# Revit family: Economy_Static_Shelving
name_source: partatom
category: Furniture
revit_build: Autodesk Revit 2016 (Build: 20150714_1515(x64)
units: mm (PartAtom-declared; Revit-internal decimal feet)

## family parameters
Always vertical = Yes
Cut with Voids When Loaded = No
OmniClass Number = 23.40.20.00
OmniClass Title = General Furniture and Specialties
Room Calculation Point = No
Shared = No
Work Plane-Based = No

## types (32) — shared parameters
Manufacturer = BISLEY
Model = Economy Shelving

## per-type parameters (varying)
| type | Depth | Extension | Extension width | Height | Shelving spacing | Width |
| 0818ESSTK30 | 300 mm | No | 800 mm  [stored 2.62467 ft] | 1832 mm  [stored 6.0105 ft] | 333 mm | 832 mm |
| 0818ESSTK30 + 0818ESEXK30 | 300 mm | Yes | 800 mm  [stored 2.62467 ft] | 1832 mm  [stored 6.0105 ft] | 333 mm | 832 mm |
| 0822ESSTK30 | 300 mm | No | 800 mm  [stored 2.62467 ft] | 2192 mm  [stored 7.1916 ft] | 405 mm | 832 mm |
| 0822ESSTK30 + 0822ESEXK30 | 300 mm | Yes | 800 mm  [stored 2.62467 ft] | 2192 mm  [stored 7.1916 ft] | 405 mm | 832 mm |
| 0818ESSTK36 | 360 mm  [stored 1.1811 ft] | No | 800 mm  [stored 2.62467 ft] | 1832 mm  [stored 6.0105 ft] | 333 mm | 832 mm |
| 0818ESSTK36 + 0818ESEXK36 | 360 mm  [stored 1.1811 ft] | Yes | 800 mm  [stored 2.62467 ft] | 1832 mm  [stored 6.0105 ft] | 333 mm | 832 mm |
| 0822ESSTK36 | 360 mm  [stored 1.1811 ft] | No | 800 mm  [stored 2.62467 ft] | 2192 mm  [stored 7.1916 ft] | 405 mm | 832 mm |
| 0822ESSTK36 + 0822ESEXK36 | 360 mm  [stored 1.1811 ft] | Yes | 800 mm  [stored 2.62467 ft] | 2192 mm  [stored 7.1916 ft] | 405 mm | 832 mm |
| 0818ESSTK40 | 400 mm  [stored 1.31234 ft] | No | 800 mm  [stored 2.62467 ft] | 1832 mm  [stored 6.0105 ft] | 333 mm | 832 mm |
| 0818ESSTK40 + 0818ESEXK40 | 400 mm  [stored 1.31234 ft] | Yes | 800 mm  [stored 2.62467 ft] | 1832 mm  [stored 6.0105 ft] | 333 mm | 832 mm |
| 0822ESSTK40 | 400 mm  [stored 1.31234 ft] | No | 800 mm  [stored 2.62467 ft] | 2192 mm  [stored 7.1916 ft] | 405 mm | 832 mm |
| 0822ESSTK40 + 0822ESEXK40 | 400 mm  [stored 1.31234 ft] | Yes | 800 mm  [stored 2.62467 ft] | 2192 mm  [stored 7.1916 ft] | 405 mm | 832 mm |
| 0818ESSTK46 | 460 mm  [stored 1.50919 ft] | No | 800 mm  [stored 2.62467 ft] | 1832 mm  [stored 6.0105 ft] | 333 mm | 832 mm |
| 0818ESSTK46 + 0818ESEXK46 | 460 mm  [stored 1.50919 ft] | Yes | 800 mm  [stored 2.62467 ft] | 1832 mm  [stored 6.0105 ft] | 333 mm | 832 mm |
| 0822ESSTK46 | 460 mm  [stored 1.50919 ft] | No | 800 mm  [stored 2.62467 ft] | 2192 mm  [stored 7.1916 ft] | 405 mm | 832 mm |
| 0822ESSTK46 + 0822ESEXK46 | 460 mm  [stored 1.50919 ft] | Yes | 800 mm  [stored 2.62467 ft] | 2192 mm  [stored 7.1916 ft] | 405 mm | 832 mm |
| 1018ESSTK30 | 300 mm | No | 1000 mm  [stored 3.28084 ft] | 1832 mm  [stored 6.0105 ft] | 333 mm | 1032 mm  [stored 3.38583 ft] |
| 1018ESSTK30 + 1018ESEXK30 | 300 mm | Yes | 1000 mm  [stored 3.28084 ft] | 1832 mm  [stored 6.0105 ft] | 333 mm | 1032 mm  [stored 3.38583 ft] |
| 1022ESSTK30 | 300 mm | No | 1000 mm  [stored 3.28084 ft] | 2192 mm  [stored 7.1916 ft] | 405 mm | 1032 mm  [stored 3.38583 ft] |
| 1022ESSTK30 + 1022ESEXK30 | 300 mm | Yes | 1000 mm  [stored 3.28084 ft] | 2192 mm  [stored 7.1916 ft] | 405 mm | 1032 mm  [stored 3.38583 ft] |
| 1018ESSTK36 | 360 mm  [stored 1.1811 ft] | No | 1000 mm  [stored 3.28084 ft] | 1832 mm  [stored 6.0105 ft] | 333 mm | 1032 mm  [stored 3.38583 ft] |
| 1018ESSTK36 + 1018ESEXK36 | 360 mm  [stored 1.1811 ft] | Yes | 1000 mm  [stored 3.28084 ft] | 1832 mm  [stored 6.0105 ft] | 333 mm | 1032 mm  [stored 3.38583 ft] |
| 1022ESSTK36 | 360 mm  [stored 1.1811 ft] | No | 1000 mm  [stored 3.28084 ft] | 2192 mm  [stored 7.1916 ft] | 405 mm | 1032 mm  [stored 3.38583 ft] |
| 1022ESSTK36 + 1022ESEXK36 | 360 mm  [stored 1.1811 ft] | Yes | 1000 mm  [stored 3.28084 ft] | 2192 mm  [stored 7.1916 ft] | 405 mm | 1032 mm  [stored 3.38583 ft] |
| 1018ESSTK40 | 400 mm  [stored 1.31234 ft] | No | 1000 mm  [stored 3.28084 ft] | 1832 mm  [stored 6.0105 ft] | 333 mm | 1032 mm  [stored 3.38583 ft] |
| 1018ESSTK40 + 1018ESEXK40 | 400 mm  [stored 1.31234 ft] | Yes | 1000 mm  [stored 3.28084 ft] | 1832 mm  [stored 6.0105 ft] | 333 mm | 1032 mm  [stored 3.38583 ft] |
| 1022ESSTK40 | 400 mm  [stored 1.31234 ft] | No | 1000 mm  [stored 3.28084 ft] | 2192 mm  [stored 7.1916 ft] | 405 mm | 1032 mm  [stored 3.38583 ft] |
| 1022ESSTK40 + 1022ESEXK40 | 400 mm  [stored 1.31234 ft] | Yes | 1000 mm  [stored 3.28084 ft] | 2192 mm  [stored 7.1916 ft] | 405 mm | 1032 mm  [stored 3.38583 ft] |
| 1018ESSTK46 | 460 mm  [stored 1.50919 ft] | No | 1000 mm  [stored 3.28084 ft] | 1832 mm  [stored 6.0105 ft] | 333 mm | 1032 mm  [stored 3.38583 ft] |
| 1018ESSTK46 + 1018ESEXK46 | 460 mm  [stored 1.50919 ft] | Yes | 1000 mm  [stored 3.28084 ft] | 1832 mm  [stored 6.0105 ft] | 333 mm | 1032 mm  [stored 3.38583 ft] |
| 1022ESSTK46 | 460 mm  [stored 1.50919 ft] | No | 1000 mm  [stored 3.28084 ft] | 2192 mm  [stored 7.1916 ft] | 405 mm | 1032 mm  [stored 3.38583 ft] |
| 1022ESSTK46 + 1022ESEXK46 | 460 mm  [stored 1.50919 ft] | Yes | 1000 mm  [stored 3.28084 ft] | 2192 mm  [stored 7.1916 ft] | 405 mm | 1032 mm  [stored 3.38583 ft] |

note: [stored X ft] marks values corroborated as IEEE doubles in the binary element streams (Revit-internal decimal feet)

## geometry (parser evidence)
native form markers: Sweep x1
no freeform markers — native parametric forms only
